# Revit family: Keilhauer_Pact_Bench_Back_77111
name_source: partatom
category: Furniture
revit_build: Autodesk Revit 2017 (Build: 20160225_1515(x64)
units: mm (PartAtom-declared; Revit-internal decimal feet)

## family parameters
Always vertical = Yes
Cut with Voids When Loaded = No
OmniClass Number = 23.40.70.14.64.11
OmniClass Title = Office Furniture
Room Calculation Point = No
Shared = No
Work Plane-Based = No

## types (4) — shared parameters
Assembly Code = E2020200
Catalog = Pact
Manufacturer = Keilhauer, Corp.
Product Documentation Link = http://www.keilhauer.com
URL = http://www.keilhauer.com

## per-type parameters (varying)
| type | Description | Length | Model | Type |
| 84" bench | Pact 84" bench back | 40.608 " | 77131 | 4 |
| 72" bench | Pact 72" bench back | 34.358 " | 77121 | 3 |
| 57" bench | Pact 57" bench back | 26.858 " | 77111 | 2 |
| 32" bench | Pact 32" bench back | 14.358 " | 77101 | 1 |

## geometry (parser evidence)
native form markers: Sweep x2
no freeform markers — native parametric forms only
